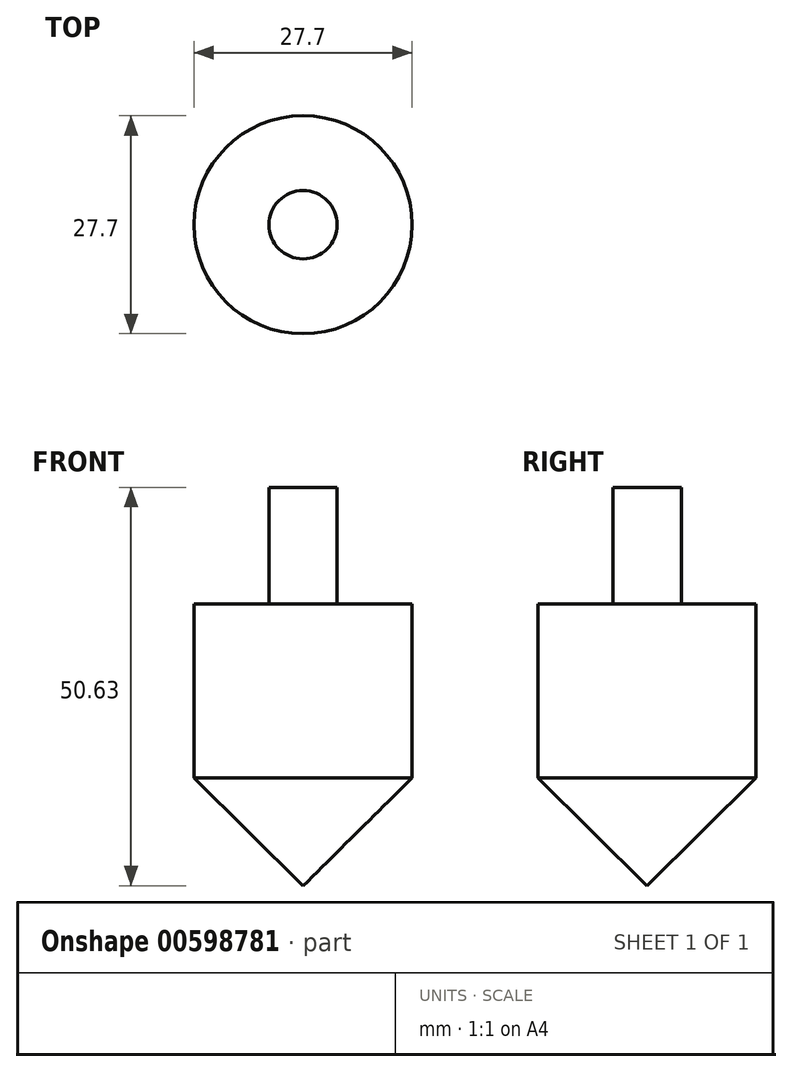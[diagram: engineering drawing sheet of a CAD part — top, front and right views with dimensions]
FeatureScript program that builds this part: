
annotation { "Feature Type Name" : "Feature", "Feature Type Description" : "" }
export const myFeature = defineFeature(function(context is Context, id is Id, definition is map)
    precondition{}
    {
        {
            var Q0;
            Q0=qCreatedBy(makeId("Front.planeOp"),FACE);
            var sketch = newSketch(context, id + "F0", { "sketchPlane" : qUnion([Q0])});
            skLineSegment(sketch, "E0", {"start": v(0, 43.78) * mm, "end": v(4.34, 43.78) * mm});
            skLineSegment(sketch, "E1", {"start": v(4.34, 43.78) * mm, "end": v(4.34, 28.95) * mm});
            skLineSegment(sketch, "E2", {"start": v(4.34, 28.95) * mm, "end": v(13.85, 28.95) * mm});
            skLineSegment(sketch, "E3", {"start": v(13.85, 28.95) * mm, "end": v(13.85, 6.85) * mm});
            skLineSegment(sketch, "E4", {"start": v(13.85, 6.85) * mm, "end": v(0, -6.85) * mm});
            skLineSegment(sketch, "E5", {"start": v(0, -6.85) * mm, "end": v(0, 43.78) * mm});
            skSolve(sketch);
        }
        {
            var Q0;
            Q0=makeQuery(id+"F0.imprint","IMPRINT",FACE,{"disambiguationData":[TD([[makeQuery(id+"F0.imprint","IMPRINT",EDGE,{"derivedFrom":sQuery(id+"F0.wireOp",EDGE,"E0")}),-1.0]])]});
            var Q1;
            Q1=sQuery(id+"F0.wireOp",EDGE,"E5");
            revolve(context, id + "F1", {"entities" : qUnion([Q0]), "axis" : qUnion([Q1]), "revolveType" : RevolveType.FULL});
        }
    });
